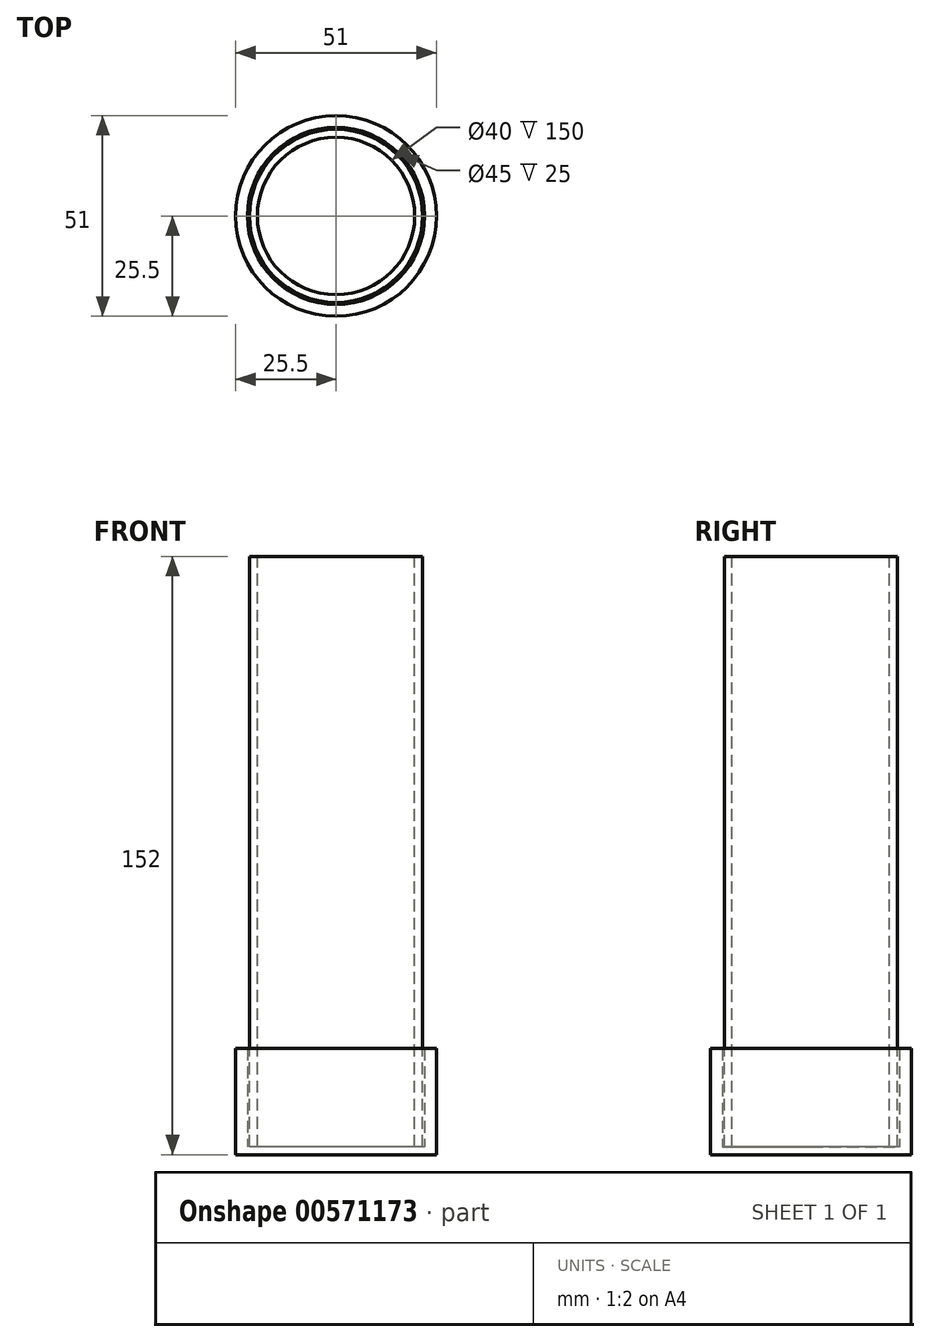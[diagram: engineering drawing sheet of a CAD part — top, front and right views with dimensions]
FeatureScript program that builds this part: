
annotation { "Feature Type Name" : "Feature", "Feature Type Description" : "" }
export const myFeature = defineFeature(function(context is Context, id is Id, definition is map)
    precondition{}
    {
        {
            var Q0;
            Q0=qCreatedBy(makeId("Front.planeOp"),FACE);
            var sketch = newSketch(context, id + "F0", { "sketchPlane" : qUnion([Q0])});
            skLineSegment(sketch, "E0", {"start": v(0, 172.83) * mm, "end": v(0, -197.58) * mm, "construction": true});
            skLineSegment(sketch, "E1", {"start": v(-208.43, 0) * mm, "end": v(198.15, 0) * mm, "construction": true});
            skLineSegment(sketch, "E2", {"start": v(20, 0) * mm, "end": v(20, 150) * mm});
            skLineSegment(sketch, "E3", {"start": v(20, 150) * mm, "end": v(22, 150) * mm});
            skLineSegment(sketch, "E4", {"start": v(22, 150) * mm, "end": v(22, 0) * mm});
            skLineSegment(sketch, "E5", {"start": v(22, 0) * mm, "end": v(20, 0) * mm});
            skSolve(sketch);
        }
        {
            var Q0;
            Q0=qSketchRegion(id+"F0",true);
            var Q1;
            Q1=sQuery(id+"F0.wireOp",EDGE,"E0");
            revolve(context, id + "F1", {"entities" : qUnion([Q0]), "axis" : qUnion([Q1]), "revolveType" : RevolveType.FULL});
        }
        {
            var Q0;
            Q0=qCreatedBy(makeId("Front.planeOp"),FACE);
            var sketch = newSketch(context, id + "F2", { "sketchPlane" : qUnion([Q0])});
            skPoint(sketch, "E6", {"position": v(16, 188.5) * mm});
            skPoint(sketch, "E7", {"position": v(22, 108.5) * mm});
            skLineSegment(sketch, "E8", {"start": v(62.19, 108.5) * mm, "end": v(25, 108.5) * mm});
            skLineSegment(sketch, "E9", {"start": v(16, 188.5) * mm, "end": v(14, 188.5) * mm});
            skLineSegment(sketch, "E10", {"start": v(62.19, 110.5) * mm, "end": v(25, 110.5) * mm});
            skPoint(sketch, "E11", {"position": v(25, 110.5) * mm});
            skLineSegment(sketch, "E12", {"start": v(25, 110.5) * mm, "end": v(25, 108.5) * mm});
            skPoint(sketch, "E13.start.orphan", {"position": v(22, 110.5) * mm});
            skLineSegment(sketch, "E14", {"start": v(0, 193.45) * mm, "end": v(0, -66.14) * mm, "construction": true});
            skLineSegment(sketch, "E15", {"start": v(62.19, 110.5) * mm, "end": v(62.19, 108.5) * mm});
            skSolve(sketch);
        }
        {
            var Q0;
            Q0=qCreatedBy(makeId("Top.planeOp"),FACE);
            var sketch = newSketch(context, id + "F3", { "sketchPlane" : qUnion([Q0])});
            skCircle(sketch, "E16", {"center": v(0, 0) * mm, "radius": 22.5 * mm});
            skCircle(sketch, "E17.0", {"center": v(0, 0) * mm, "radius": 25.5 * mm});
            skSolve(sketch);
        }
        {
            var Q0;
            Q0=qSketchRegion(id+"F3",true);
            extrude(context, id + "F4", {"entities" : qUnion([Q0]), "depth" : 25 * mm, "offsetDistance" : 25 * mm});
        }
        {
            var Q0;
            Q0=makeQuery(id+"F4.opExtrude","CAP_FACE",FACE,{"disambiguationData":[OSD([sQuery(id+"F3.wireOp",EDGE,"E16"),sQuery(id+"F3.wireOp",EDGE,"E17.0")])],"isStart":true});
            var sketch = newSketch(context, id + "F5", { "sketchPlane" : qUnion([Q0])});
            skCircle(sketch, "E18.0", {"center": v(0, 0) * mm, "radius": 25.5 * mm});
            skSolve(sketch);
        }
        {
            var Q0;
            Q0=qSketchRegion(id+"F5",true);
            extrude(context, id + "F6", {"entities" : qUnion([Q0]), "operationType" : NewBodyOperationType.ADD, "depth" : 2 * mm, "offsetDistance" : 25 * mm});
        }
        {
            var Q0;
            Q0=qCreatedBy(makeId("Top.planeOp"),FACE);
            cPlane(context, id + "F7", {"entities" : qUnion([Q0]), "cplaneType" : CPlaneType.OFFSET, "offset" : 110.5 * mm, "width" : 150 * mm, "height" : 150 * mm});
        }
        {
            var Q0;
            Q0=qCreatedBy(id+"F7.planeOp",FACE);
            cPlane(context, id + "F8", {"entities" : qUnion([Q0]), "cplaneType" : CPlaneType.OFFSET, "offset" : 80 * mm, "width" : 150 * mm, "height" : 150 * mm});
        }
    });
